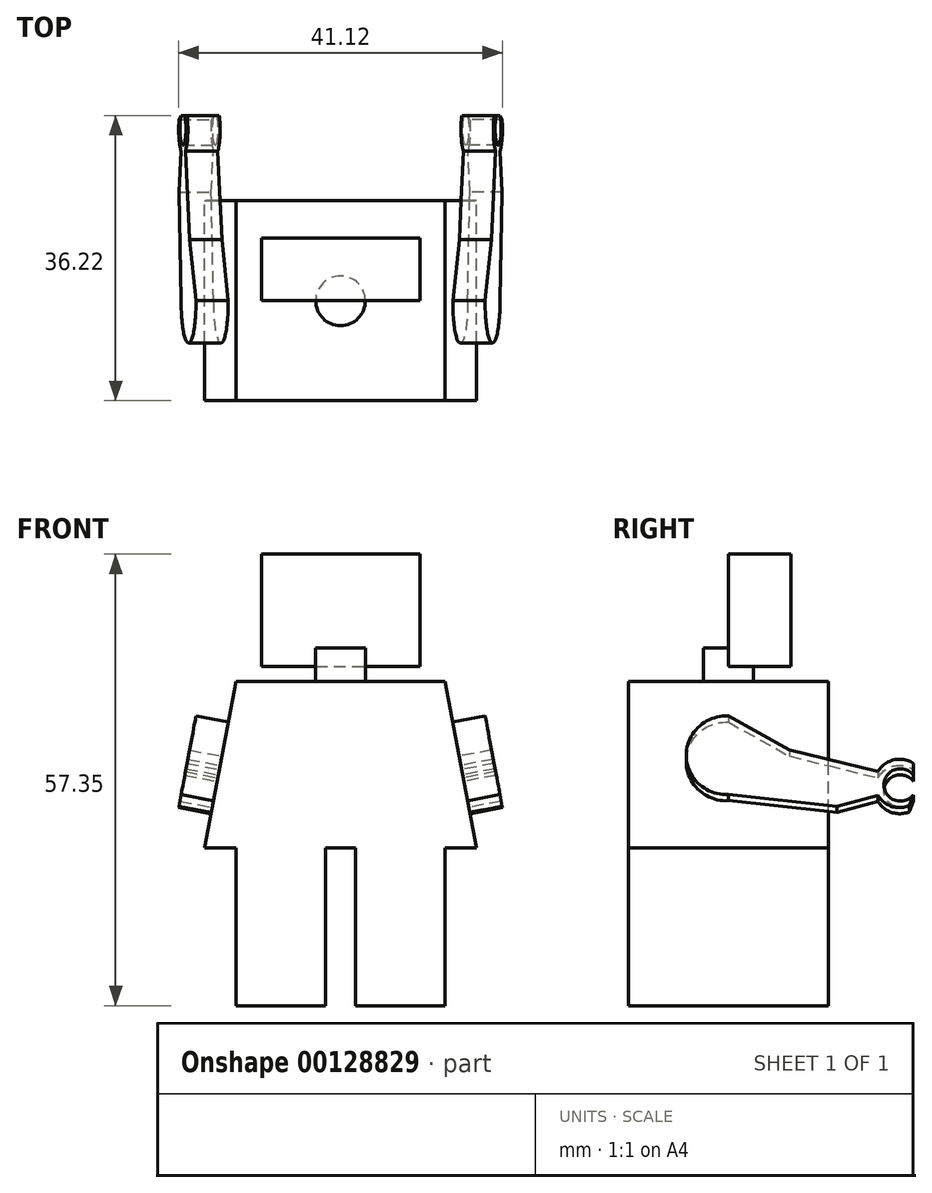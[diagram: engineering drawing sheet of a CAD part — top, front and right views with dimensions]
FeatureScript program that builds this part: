
annotation { "Feature Type Name" : "Feature", "Feature Type Description" : "" }
export const myFeature = defineFeature(function(context is Context, id is Id, definition is map)
    precondition{}
    {
        {
            var Q0;
            Q0=qCreatedBy(makeId("Front.planeOp"),FACE);
            var sketch = newSketch(context, id + "F0", { "sketchPlane" : qUnion([Q0])});
            skLineSegment(sketch, "E0", {"start": v(-17.27, 0) * mm, "end": v(-13.29, 21.17) * mm});
            skLineSegment(sketch, "E1", {"start": v(-13.29, 21.17) * mm, "end": v(0, 21.17) * mm});
            skLineSegment(sketch, "E2", {"start": v(0, 21.17) * mm, "end": v(0, 0) * mm});
            skLineSegment(sketch, "E3", {"start": v(0, 0) * mm, "end": v(-17.27, 0) * mm});
            skLineSegment(sketch, "E4.bottom", {"start": v(-13.29, 0) * mm, "end": v(-1.88, 0) * mm});
            skLineSegment(sketch, "E4.top", {"start": v(-13.29, -20.05) * mm, "end": v(-1.88, -20.05) * mm});
            skLineSegment(sketch, "E4.left", {"start": v(-13.29, 0) * mm, "end": v(-13.29, -20.05) * mm});
            skLineSegment(sketch, "E4.right", {"start": v(-1.88, 0) * mm, "end": v(-1.88, -20.05) * mm});
            skLineSegment(sketch, "E5.MirrorCS", {"start": v(13.29, 21.17) * mm, "end": v(0, 21.17) * mm});
            skLineSegment(sketch, "E6.MirrorCS", {"start": v(17.27, 0) * mm, "end": v(13.29, 21.17) * mm});
            skLineSegment(sketch, "E7.MirrorCS", {"start": v(0, 0) * mm, "end": v(17.27, 0) * mm});
            skLineSegment(sketch, "E8.MirrorCS", {"start": v(1.88, 0) * mm, "end": v(1.88, -20.05) * mm});
            skLineSegment(sketch, "E9.MirrorCS", {"start": v(13.29, 0) * mm, "end": v(13.29, -20.05) * mm});
            skLineSegment(sketch, "E10.MirrorCS", {"start": v(13.29, -20.05) * mm, "end": v(1.88, -20.05) * mm});
            skSolve(sketch);
        }
        {
            var Q0;
            Q0 = qSketchRegion(id + "F0", true);
            extrude(context, id + "F1", {"entities" : qUnion([Q0]), "endBound" : BoundingType.SYMMETRIC, "depth" : 25.4 * mm});
        }
        {
            var Q0;
            Q0=makeQuery(id+"F1.opExtrude","SWEPT_FACE",FACE,{"disambiguationData":[OSD([sQuery(id+"F0.wireOp",EDGE,"E0")])]});
            var sketch = newSketch(context, id + "F2", { "sketchPlane" : qUnion([Q0])});
            skArc(sketch, "E11", {"start": v(0, 2.9) * mm, "mid": v(5.35, 7.98) * mm, "end": v(0, 13.05) * mm});
            skLineSegment(sketch, "E12", {"start": v(0, 13.05) * mm, "end": v(-7.76, 8.66) * mm});
            skLineSegment(sketch, "E13", {"start": v(-7.76, 8.66) * mm, "end": v(-19.1, 5.84) * mm});
            skLineSegment(sketch, "E14", {"start": v(0, 2.9) * mm, "end": v(-13.8, 1.4) * mm});
            skLineSegment(sketch, "E15", {"start": v(-13.8, 1.4) * mm, "end": v(-19.03, 2.8) * mm});
            skArc(sketch, "E16", {"start": v(-23.03, 1.48) * mm, "mid": v(-18.63, 4.63) * mm, "end": v(-23.52, 6.93) * mm});
            skArc(sketch, "E17", {"start": v(-23.52, 2.88) * mm, "mid": v(-19.76, 4.14) * mm, "end": v(-23.52, 5.4) * mm});
            skLineSegment(sketch, "E18", {"start": v(-23.52, 5.4) * mm, "end": v(-23.52, 6.93) * mm});
            skLineSegment(sketch, "E19", {"start": v(-23.52, 2.88) * mm, "end": v(-23.03, 1.48) * mm});
            skSolve(sketch);
        }
        {
            var Q0;
            Q0 = qSketchRegion(id + "F2", true);
            extrude(context, id + "F3", {"entities" : qUnion([Q0]), "operationType" : NewBodyOperationType.ADD, "depth" : 4.17 * mm});
        }
        {
            var Q0;
            Q0=makeQuery(id+"F1.opExtrude","SWEPT_BODY",BODY,{"disambiguationData":[OSD([sQuery(id+"F0.wireOp",EDGE,"E0"),sQuery(id+"F0.wireOp",EDGE,"E1"),sQuery(id+"F0.wireOp",EDGE,"E3"),sQuery(id+"F0.wireOp",EDGE,"E4.top"),sQuery(id+"F0.wireOp",EDGE,"E4.left"),sQuery(id+"F0.wireOp",EDGE,"E4.right"),sQuery(id+"F0.wireOp",EDGE,"E5.MirrorCS"),sQuery(id+"F0.wireOp",EDGE,"E6.MirrorCS"),sQuery(id+"F0.wireOp",EDGE,"E7.MirrorCS"),sQuery(id+"F0.wireOp",EDGE,"E8.MirrorCS"),sQuery(id+"F0.wireOp",EDGE,"E9.MirrorCS"),sQuery(id+"F0.wireOp",EDGE,"E10.MirrorCS")])]});
            var Q1;
            Q1=qCreatedBy(makeId("Right.planeOp"),FACE);
            mirror(context, id + "F4", {"operationType" : NewBodyOperationType.ADD, "entities" : qUnion([Q0]), "mirrorPlane" : qUnion([Q1])});
        }
        {
            var Q0;
            Q0=qCreatedBy(makeId("Top.planeOp"),FACE);
            var sketch = newSketch(context, id + "F5", { "sketchPlane" : qUnion([Q0])});
            skCircle(sketch, "E20", {"center": v(0, 0) * mm, "radius": 3.15 * mm});
            skSolve(sketch);
        }
        {
            var Q0;
            Q0 = qSketchRegion(id + "F5", true);
            extrude(context, id + "F6", {"entities" : qUnion([Q0]), "operationType" : NewBodyOperationType.ADD, "depth" : 25.4 * mm});
        }
        {
            var Q0;
            Q0=qCreatedBy(makeId("Front.planeOp"),FACE);
            var sketch = newSketch(context, id + "F7", { "sketchPlane" : qUnion([Q0])});
            skLineSegment(sketch, "E21.bottom", {"start": v(0, 23.06) * mm, "end": v(10.06, 23.06) * mm});
            skLineSegment(sketch, "E21.top", {"start": v(0, 37.3) * mm, "end": v(10.06, 37.3) * mm});
            skLineSegment(sketch, "E21.left", {"start": v(0, 23.06) * mm, "end": v(0, 37.3) * mm});
            skLineSegment(sketch, "E21.right", {"start": v(10.06, 23.06) * mm, "end": v(10.06, 37.3) * mm});
            skLineSegment(sketch, "E22.MirrorCS", {"start": v(0, 23.06) * mm, "end": v(-10.06, 23.06) * mm});
            skLineSegment(sketch, "E23.MirrorCS", {"start": v(-10.06, 23.06) * mm, "end": v(-10.06, 37.3) * mm});
            skLineSegment(sketch, "E24.MirrorCS", {"start": v(0, 37.3) * mm, "end": v(-10.06, 37.3) * mm});
            skSolve(sketch);
        }
        {
            var Q0;
            Q0 = qSketchRegion(id + "F7", true);
            extrude(context, id + "F8", {"entities" : qUnion([Q0]), "operationType" : NewBodyOperationType.ADD, "oppositeDirection" : true, "depth" : 7.96 * mm});
        }
    });
